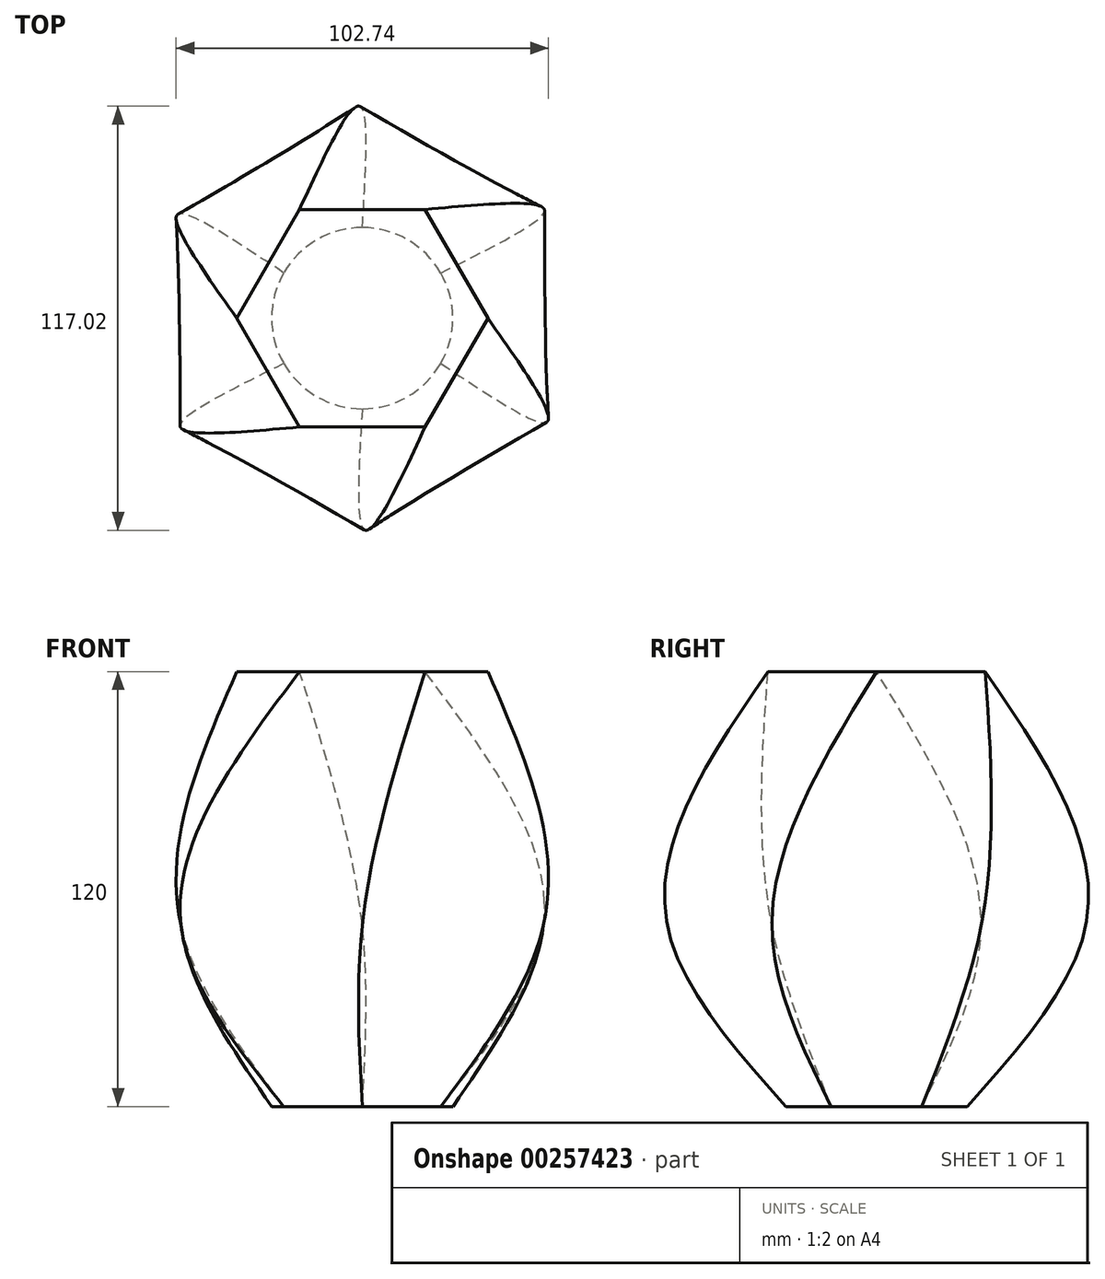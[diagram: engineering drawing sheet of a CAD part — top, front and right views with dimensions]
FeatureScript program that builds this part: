
annotation { "Feature Type Name" : "Feature", "Feature Type Description" : "" }
export const myFeature = defineFeature(function(context is Context, id is Id, definition is map)
    precondition{}
    {
        {
            var Q0;
            Q0=qCreatedBy(makeId("Top.planeOp"),FACE);
            var sketch = newSketch(context, id + "F0", { "sketchPlane" : qUnion([Q0])});
            skCircle(sketch, "E0", {"center": v(0, 0) * mm, "radius": 25 * mm});
            skSolve(sketch);
        }
        {
            var Q0;
            Q0=makeQuery(id+"F0.imprint","IMPRINT",FACE,{"disambiguationData":[TD([[makeQuery(id+"F0.imprint","IMPRINT",EDGE,{"derivedFrom":sQuery(id+"F0.wireOp",EDGE,"E0")}),1.0]])]});
            cPlane(context, id + "F1", {"entities" : qUnion([Q0]), "cplaneType" : CPlaneType.OFFSET, "offset" : 50 * mm, "width" : 150 * mm, "height" : 150 * mm});
        }
        {
            var Q0;
            Q0=qCreatedBy(id+"F1.planeOp",FACE);
            var sketch = newSketch(context, id + "F2", { "sketchPlane" : qUnion([Q0])});
            skCircle(sketch, "E1.cCircle", {"center": v(0, 0) * mm, "radius": 50 * mm, "construction": true});
            skLineSegment(sketch, "E1.0", {"start": v(-50, 28.87) * mm, "end": v(0, 57.74) * mm});
            skLineSegment(sketch, "E1.1", {"start": v(0, 57.74) * mm, "end": v(50, 28.87) * mm});
            skLineSegment(sketch, "E1.2", {"start": v(50, 28.87) * mm, "end": v(50, -28.87) * mm});
            skLineSegment(sketch, "E1.3", {"start": v(50, -28.87) * mm, "end": v(0, -57.74) * mm});
            skLineSegment(sketch, "E1.4", {"start": v(0, -57.74) * mm, "end": v(-50, -28.87) * mm});
            skLineSegment(sketch, "E1.5", {"start": v(-50, -28.87) * mm, "end": v(-50, 28.87) * mm});
            skPoint(sketch, "E1.0.midPoint", {"position": v(-25, 43.3) * mm});
            skSolve(sketch);
        }
        {
            var Q0;
            Q0=makeQuery(id+"F2.imprint","IMPRINT",FACE,{"disambiguationData":[TD([[makeQuery(id+"F2.imprint","IMPRINT",EDGE,{"derivedFrom":sQuery(id+"F2.wireOp",EDGE,"E1.0")}),-1.0]])]});
            cPlane(context, id + "F3", {"entities" : qUnion([Q0]), "cplaneType" : CPlaneType.OFFSET, "offset" : 70 * mm, "width" : 150 * mm, "height" : 150 * mm});
        }
        {
            var Q0;
            Q0=qCreatedBy(id+"F3.planeOp",FACE);
            var sketch = newSketch(context, id + "F4", { "sketchPlane" : qUnion([Q0])});
            skCircle(sketch, "E2.cCircle", {"center": v(0, 0) * mm, "radius": 30 * mm, "construction": true});
            skLineSegment(sketch, "E2.0", {"start": v(-17.32, 30) * mm, "end": v(17.32, 30) * mm});
            skLineSegment(sketch, "E2.1", {"start": v(17.32, 30) * mm, "end": v(34.64, 0) * mm});
            skLineSegment(sketch, "E2.2", {"start": v(34.64, 0) * mm, "end": v(17.32, -30) * mm});
            skLineSegment(sketch, "E2.3", {"start": v(17.32, -30) * mm, "end": v(-17.32, -30) * mm});
            skLineSegment(sketch, "E2.4", {"start": v(-17.32, -30) * mm, "end": v(-34.64, 0) * mm});
            skLineSegment(sketch, "E2.5", {"start": v(-34.64, 0) * mm, "end": v(-17.32, 30) * mm});
            skPoint(sketch, "E2.0.midPoint", {"position": v(0, 30) * mm});
            skSolve(sketch);
        }
        {
            var Q0;
            Q0=makeQuery(id+"F0.imprint","IMPRINT",FACE,{"disambiguationData":[TD([[makeQuery(id+"F0.imprint","IMPRINT",EDGE,{"derivedFrom":sQuery(id+"F0.wireOp",EDGE,"E0")}),1.0]])]});
            var Q1;
            Q1=makeQuery(id+"F2.imprint","IMPRINT",FACE,{"disambiguationData":[TD([[makeQuery(id+"F2.imprint","IMPRINT",EDGE,{"derivedFrom":sQuery(id+"F2.wireOp",EDGE,"E1.0")}),-1.0]])]});
            var Q2;
            Q2=makeQuery(id+"F4.imprint","IMPRINT",FACE,{"disambiguationData":[TD([[makeQuery(id+"F4.imprint","IMPRINT",EDGE,{"derivedFrom":sQuery(id+"F4.wireOp",EDGE,"E2.0")}),-1.0]])]});
            loft(context, id + "F5", {"sheetProfilesArray" : [{ "sheetProfileEntities" : qUnion([Q0]) }, { "sheetProfileEntities" : qUnion([Q1]) }, { "sheetProfileEntities" : qUnion([Q2]) }]});
        }
    });
